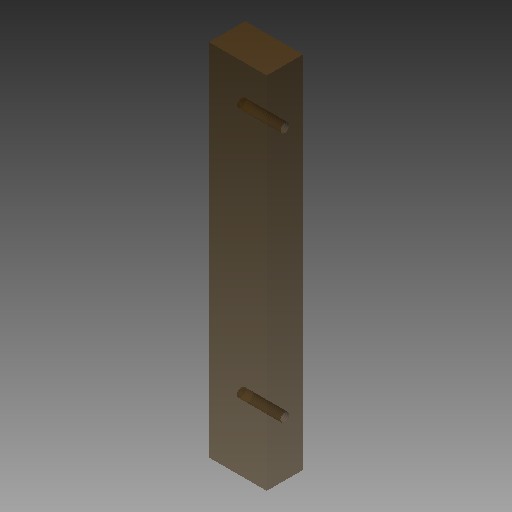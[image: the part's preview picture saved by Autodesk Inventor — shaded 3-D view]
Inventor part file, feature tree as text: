
AUTODESK INVENTOR PART (.ipt)
format: ipt  version: 2018 (Build 220112000, 112)  size: 93,696 bytes
history: native  units: mm
features: extrude x1, hole x1
ambient origin geometry x8: Origin, YZ Plane, XZ Plane, XY Plane, X Axis, Y Axis, Z Axis, Center Point
bodies: Volumenkörper1 (feature_tree)
feature tree (2):
  extrude  "Extrusion1"  Depth=15.9mm
  hole  "Bohrung1"  [1 undecoded]
note: 1 required parameter value undecoded (feature->parameter linkage not recoverable at this tier; creation-order binding heuristic only, values carry confidence <= 0.55)
